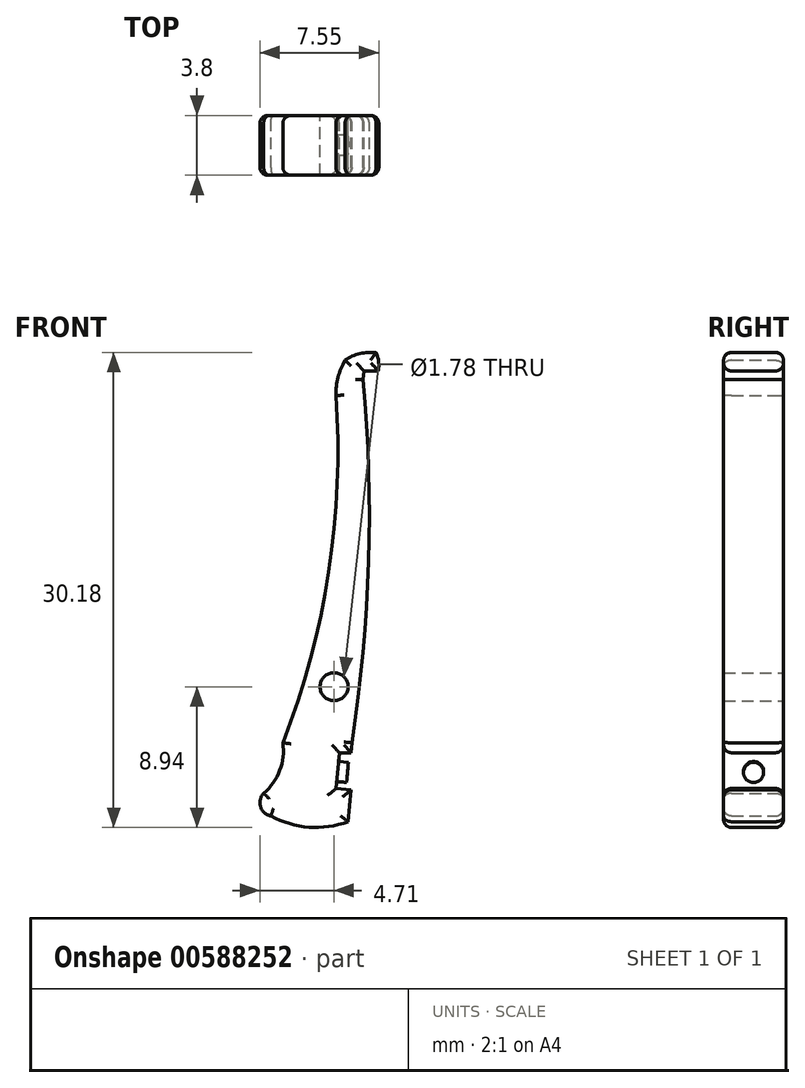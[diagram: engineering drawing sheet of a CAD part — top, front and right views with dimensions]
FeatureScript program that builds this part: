
annotation { "Feature Type Name" : "Feature", "Feature Type Description" : "" }
export const myFeature = defineFeature(function(context is Context, id is Id, definition is map)
    precondition{}
    {
        {
            var Q0;
            Q0=qCreatedBy(makeId("Front.planeOp"),FACE);
            var sketch = newSketch(context, id + "F0", { "sketchPlane" : qUnion([Q0])});
            skPoint(sketch, "E0.startSnap0", {"position": v(-25.9, 31.9) * mm});
            skArc(sketch, "E1", {"start": v(-31.05, 8.39) * mm, "mid": v(-28.64, 7.68) * mm, "end": v(-26.14, 8.03) * mm});
            skPoint(sketch, "E2", {"position": v(-27.03, 16.6) * mm});
            skArc(sketch, "E3", {"start": v(-24.36, 37.82) * mm, "mid": v(-25.39, 37.76) * mm, "end": v(-26.33, 37.34) * mm});
            skArc(sketch, "E4", {"start": v(-25.9, 13.04) * mm, "mid": v(-24.84, 24.56) * mm, "end": v(-25.18, 36.11) * mm});
            skArc(sketch, "E5", {"start": v(-31.5, 9.84) * mm, "mid": v(-31.7, 8.99) * mm, "end": v(-31.05, 8.39) * mm});
            skArc(sketch, "E6", {"start": v(-31.5, 9.84) * mm, "mid": v(-30.48, 11.29) * mm, "end": v(-30.28, 13.04) * mm});
            skArc(sketch, "E7", {"start": v(-30.28, 13.04) * mm, "mid": v(-27.37, 23.88) * mm, "end": v(-26.91, 35.1) * mm});
            skLineSegment(sketch, "E8", {"start": v(-25.9, 13.04) * mm, "end": v(-25.94, 12.41) * mm});
            skLineSegment(sketch, "E9", {"start": v(-25.94, 12.41) * mm, "end": v(-26.7, 12.41) * mm});
            skLineSegment(sketch, "E10", {"start": v(-26.7, 12.41) * mm, "end": v(-26.9, 10.14) * mm});
            skLineSegment(sketch, "E11", {"start": v(-26.9, 10.14) * mm, "end": v(-25.94, 10.05) * mm});
            skLineSegment(sketch, "E12", {"start": v(-25.94, 10.05) * mm, "end": v(-26.14, 8.03) * mm});
            skArc(sketch, "E13", {"start": v(-26.33, 37.34) * mm, "mid": v(-26.78, 36.26) * mm, "end": v(-26.91, 35.1) * mm});
            skLineSegment(sketch, "E14", {"start": v(-24.23, 36.66) * mm, "end": v(-25.14, 36.66) * mm});
            skLineSegment(sketch, "E15", {"start": v(-25.14, 36.66) * mm, "end": v(-25.18, 36.11) * mm});
            skArc(sketch, "E16", {"start": v(-24.23, 36.66) * mm, "mid": v(-24.2, 37.25) * mm, "end": v(-24.36, 37.82) * mm});
            skSolve(sketch);
        }
        {
            var Q0;
            Q0=makeQuery(id+"F0.imprint","IMPRINT",FACE,{"disambiguationData":[TD([[makeQuery(id+"F0.imprint","IMPRINT",EDGE,{"derivedFrom":sQuery(id+"F0.wireOp",EDGE,"TBWAcwC6-k6ig-hbxc-4Lqx-uheGlr5LRosn")}),-1.0]])]});
            var Q1;
            Q1=makeQuery(id+"F0.imprint","IMPRINT",FACE,{"disambiguationData":[TD([[makeQuery(id+"F0.imprint","IMPRINT",EDGE,{"derivedFrom":sQuery(id+"F0.wireOp",EDGE,"SmL4iVBr-4pmG-SiZn-LyIa-iLHiD0tTn9LW")}),-1.0]])]});
            var Q2;
            Q2=makeQuery(id+"F0.imprint","IMPRINT",FACE,{"disambiguationData":[TD([[makeQuery(id+"F0.imprint","IMPRINT",EDGE,{"derivedFrom":sQuery(id+"F0.wireOp",EDGE,"DZ0YGsYz-GWPH-AjaK-bXoq-g6o46ZnLfoYJ")}),1.0]])]});
            var Q3;
            Q3=makeQuery(id+"F0.imprint","IMPRINT",FACE,{"disambiguationData":[TD([[makeQuery(id+"F0.imprint","IMPRINT",EDGE,{"derivedFrom":sQuery(id+"F0.wireOp",EDGE,"E0")}),1.0]])]});
            var Q4;
            Q4=makeQuery(id+"F0.imprint","IMPRINT",FACE,{"disambiguationData":[TD([[makeQuery(id+"F0.imprint","IMPRINT",EDGE,{"derivedFrom":sQuery(id+"F0.wireOp",EDGE,"E1")}),1.0]])]});
            extrude(context, id + "F1", {"entities" : qUnion([Q0, Q1, Q2, Q3, Q4]), "depth" : 3.8 * mm, "offsetDistance" : 25.4 * mm});
        }
        {
            var Q0;
            Q0=makeQuery(id+"F1.opExtrude","CAP_FACE",FACE,{"disambiguationData":[OSD([sQuery(id+"F0.wireOp",EDGE,"TBWAcwC6-k6ig-hbxc-4Lqx-uheGlr5LRosn"),sQuery(id+"F0.wireOp",EDGE,"SmL4iVBr-4pmG-SiZn-LyIa-iLHiD0tTn9LW"),sQuery(id+"F0.wireOp",EDGE,"Z8fLKmna-7HhA-erUR-Qk4x-3B4DOyDasTVS"),sQuery(id+"F0.wireOp",EDGE,"tXY0Dcre-mQ9i-wgZ5-Ndfu-p6JJD5JXdl3N"),sQuery(id+"F0.wireOp",EDGE,"EMTDdt1x-3t7p-S4eL-Iww4-TH66BuWMNixS"),sQuery(id+"F0.wireOp",EDGE,"DRJgoEhV-YMpq-fp7K-13kr-P5Ph3akUMdw5"),sQuery(id+"F0.wireOp",EDGE,"xViL0m00-smH0-p5U3-UlI9-gMdmjnANV09y"),sQuery(id+"F0.wireOp",EDGE,"tfQQhQ1q-Axi8-2Fwg-4l3V-BKhf0eeHV7m8")])],"isStart":false});
            var Q1;
            Q1=makeQuery(id+"F1.opExtrude","CAP_FACE",FACE,{"disambiguationData":[OSD([sQuery(id+"F0.wireOp",EDGE,"DZ0YGsYz-GWPH-AjaK-bXoq-g6o46ZnLfoYJ"),sQuery(id+"F0.wireOp",EDGE,"U7MLo9DM-UHUD-GN0G-Tsov-6Cn9oIOF7M8j"),sQuery(id+"F0.wireOp",EDGE,"E0"),sQuery(id+"F0.wireOp",EDGE,"E1"),sQuery(id+"F0.wireOp",EDGE,"Hnuc7x9z-NU25-pcE4-7chQ-k3Ju4ccaL3F8"),sQuery(id+"F0.wireOp",EDGE,"ZaCoodtV-YJy9-PjJA-dKgG-lGWemeWEPG6G"),sQuery(id+"F0.wireOp",EDGE,"9RkFXUuS-dfr7-pDPm-kiLa-5FFDreSMogIh"),sQuery(id+"F0.wireOp",EDGE,"VCwX4kx2-lgP2-9NyK-X3z6-AxeLFEWkLXW9"),sQuery(id+"F0.wireOp",EDGE,"E3"),sQuery(id+"F0.wireOp",EDGE,"JTpBRBWM-GOKF-XcNr-0ApG-fzQ2LgddEU4B"),sQuery(id+"F0.wireOp",EDGE,"DjoNHK1F-HUlz-bm2D-3Fmb-02nYqZXkhEP2")])],"isStart":false});
            fillet(context, id + "F2", {"entities" : qUnion([Q0, Q1]), "radius" : 0.5 * mm, "tangentPropagation" : true, "allowEdgeOverflow" : false});
        }
        {
            var Q0;
            Q0=makeQuery(id+"F1.opExtrude","CAP_FACE",FACE,{"disambiguationData":[OSD([sQuery(id+"F0.wireOp",EDGE,"TBWAcwC6-k6ig-hbxc-4Lqx-uheGlr5LRosn"),sQuery(id+"F0.wireOp",EDGE,"SmL4iVBr-4pmG-SiZn-LyIa-iLHiD0tTn9LW"),sQuery(id+"F0.wireOp",EDGE,"Z8fLKmna-7HhA-erUR-Qk4x-3B4DOyDasTVS"),sQuery(id+"F0.wireOp",EDGE,"tXY0Dcre-mQ9i-wgZ5-Ndfu-p6JJD5JXdl3N"),sQuery(id+"F0.wireOp",EDGE,"EMTDdt1x-3t7p-S4eL-Iww4-TH66BuWMNixS"),sQuery(id+"F0.wireOp",EDGE,"DRJgoEhV-YMpq-fp7K-13kr-P5Ph3akUMdw5"),sQuery(id+"F0.wireOp",EDGE,"xViL0m00-smH0-p5U3-UlI9-gMdmjnANV09y"),sQuery(id+"F0.wireOp",EDGE,"tfQQhQ1q-Axi8-2Fwg-4l3V-BKhf0eeHV7m8")])],"isStart":true});
            var Q1;
            Q1=makeQuery(id+"F1.opExtrude","CAP_EDGE",EDGE,{"disambiguationData":[OSD([sQuery(id+"F0.wireOp",EDGE,"U7MLo9DM-UHUD-GN0G-Tsov-6Cn9oIOF7M8j")])],"isStart":true});
            var Q2;
            Q2=makeQuery(id+"F1.opExtrude","CAP_FACE",FACE,{"disambiguationData":[OSD([sQuery(id+"F0.wireOp",EDGE,"DZ0YGsYz-GWPH-AjaK-bXoq-g6o46ZnLfoYJ"),sQuery(id+"F0.wireOp",EDGE,"U7MLo9DM-UHUD-GN0G-Tsov-6Cn9oIOF7M8j"),sQuery(id+"F0.wireOp",EDGE,"E0"),sQuery(id+"F0.wireOp",EDGE,"E1"),sQuery(id+"F0.wireOp",EDGE,"Hnuc7x9z-NU25-pcE4-7chQ-k3Ju4ccaL3F8"),sQuery(id+"F0.wireOp",EDGE,"ZaCoodtV-YJy9-PjJA-dKgG-lGWemeWEPG6G"),sQuery(id+"F0.wireOp",EDGE,"9RkFXUuS-dfr7-pDPm-kiLa-5FFDreSMogIh"),sQuery(id+"F0.wireOp",EDGE,"VCwX4kx2-lgP2-9NyK-X3z6-AxeLFEWkLXW9"),sQuery(id+"F0.wireOp",EDGE,"E3"),sQuery(id+"F0.wireOp",EDGE,"JTpBRBWM-GOKF-XcNr-0ApG-fzQ2LgddEU4B"),sQuery(id+"F0.wireOp",EDGE,"DjoNHK1F-HUlz-bm2D-3Fmb-02nYqZXkhEP2")])],"isStart":true});
            fillet(context, id + "F3", {"entities" : qUnion([Q0, Q1, Q2]), "radius" : 0.5 * mm, "tangentPropagation" : true, "allowEdgeOverflow" : false});
        }
        {
            var Q0;
            Q0=sQuery(id+"F0.wireOp",VERTEX,"E2");
            var Q1;
            Q1=makeQuery(id+"F1.opExtrude","SWEPT_BODY",BODY,{"disambiguationData":[OSD([sQuery(id+"F0.wireOp",EDGE,"SmL4iVBr-4pmG-SiZn-LyIa-iLHiD0tTn9LW"),sQuery(id+"F0.wireOp",EDGE,"DZ0YGsYz-GWPH-AjaK-bXoq-g6o46ZnLfoYJ"),sQuery(id+"F0.wireOp",EDGE,"3m026B4s-DDE8-1BRj-nvnf-oSMk3fbBo1lY"),sQuery(id+"F0.wireOp",EDGE,"lDz213EB-8Cgf-k5Re-Rzh3-vqPn5bZ67ITq"),sQuery(id+"F0.wireOp",EDGE,"MAcm5kiI-47TM-ICoB-Mq84-n1HGmDhQy0hv"),sQuery(id+"F0.wireOp",EDGE,"U7MLo9DM-UHUD-GN0G-Tsov-6Cn9oIOF7M8j"),sQuery(id+"F0.wireOp",EDGE,"E0"),sQuery(id+"F0.wireOp",EDGE,"E1"),sQuery(id+"F0.wireOp",EDGE,"Hnuc7x9z-NU25-pcE4-7chQ-k3Ju4ccaL3F8"),sQuery(id+"F0.wireOp",EDGE,"ZaCoodtV-YJy9-PjJA-dKgG-lGWemeWEPG6G")])]});
            hole(context, id + "F4", {"style" : HoleStyle.SIMPLE, "endStyle" : HoleEndStyle.THROUGH, "oppositeDirection" : true, "holeDiameter" : 1.78 * mm, "majorDiameter" : 6.35 * mm, "isTappedThrough" : true, "tappedDepth" : 12.7 * mm, "tapClearance" : 3, "locations" : qUnion([Q0]), "scope" : qUnion([Q1])});
        }
        {
            var Q0;
            Q0=makeQuery(id+"F1.opExtrude","SWEPT_FACE",FACE,{"disambiguationData":[OSD([sQuery(id+"F0.wireOp",EDGE,"E10")])]});
            var sketch = newSketch(context, id + "F5", { "sketchPlane" : qUnion([Q0])});
            skCircle(sketch, "E17", {"center": v(-1.9, 8.82) * mm, "radius": 0.64 * mm});
            skPoint(sketch, "E17.centerSnap0", {"position": v(-0.5, 8.82) * mm});
            skPoint(sketch, "E17.centerSnap1", {"position": v(-1.9, 9.96) * mm});
            skSolve(sketch);
        }
        {
            var Q0;
            Q0=makeQuery(id+"F5.imprint","IMPRINT",FACE,{"disambiguationData":[TD([[makeQuery(id+"F5.imprint","IMPRINT",EDGE,{"derivedFrom":sQuery(id+"F5.wireOp",EDGE,"E17")}),1.0]])]});
            extrude(context, id + "F6", {"entities" : qUnion([Q0]), "operationType" : NewBodyOperationType.ADD, "depth" : 0.63 * mm, "offsetDistance" : 25.4 * mm});
        }
    });
